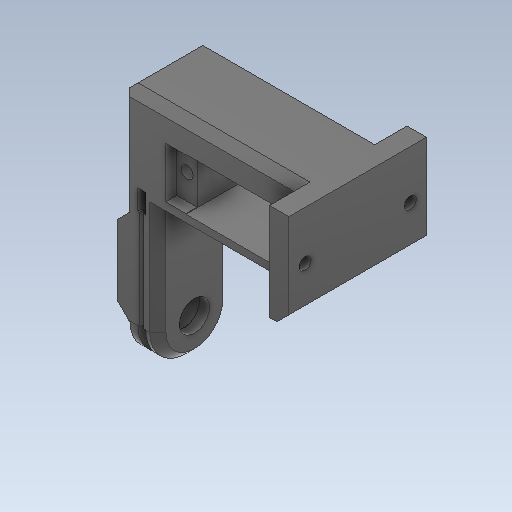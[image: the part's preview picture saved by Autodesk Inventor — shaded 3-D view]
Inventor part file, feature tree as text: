
AUTODESK INVENTOR PART (.ipt)
format: ipt  version: 2020 (Build 240168000, 168)  size: 919,552 bytes
history: native  units: mm
features: extrude x39, sketch x38, projected_geometry x26, chamfer x8, reference x8, other x5, plane x1, hole x1
ambient origin geometry x8: Origin, YZ Plane, XZ Plane, XY Plane, X Axis, Y Axis, Z Axis, Center Point
bodies: Solid1 (feature_tree)
feature tree (126):
  extrude  "Extrusion1"  Depth=45.0mm
  plane  "Work Plane1"
  extrude  "Extrusion2"  Depth=18.0mm
  extrude  "Extrusion3"  Depth=51.1mm TaperAngle=0.0deg
  extrude  "Extrusion4"  TaperAngle=0.0deg  [1 undecoded]
  extrude  "Extrusion5"  Depth=50.1mm TaperAngle=0.0deg
  sketch  "Sketch6"  dims[d14=7.199887mm d15=3.599976mm]
  extrude  "Extrusion6"  Depth=3.599976mm
  extrude  "Extrusion7"  Depth=0.15mm
  extrude  "Extrusion8"  Depth=0.15mm
  extrude  "Extrusion10"  Depth=15.9mm TaperAngle=0.0deg
  extrude  "Extrusion11"  Depth=23.15mm
  extrude  "Extrusion12"  Depth=3.925mm
  extrude  "Extrusion13"  Depth=5.15mm
  sketch  "Sketch14"  dims[d29=2.525mm d30=5.15mm]
  extrude  "Extrusion14"  Depth=12.55mm
  extrude  "Extrusion15"  Depth=2.75mm TaperAngle=0.0deg
  hole  "Hole1"  [1 undecoded]
  extrude  "Extrusion16"  Depth=2.525mm
  extrude  "Extrusion18"  Depth=23.15mm
  extrude  "Extrusion20"  Depth=10.0mm
  extrude  "Extrusion21"  Depth=0.0mm
  extrude  "Extrusion22"  TaperAngle=0.0deg  [1 undecoded]
  chamfer  "Chamfer1"  Distance=12.55mm
  chamfer  "Chamfer2"  Distance=4.0mm
  extrude  "Extrusion25"  Depth=3.85mm
  extrude  "Extrusion26"  Depth=0.765mm
  extrude  "Extrusion28"  Depth=18.0mm
  extrude  "Extrusion31"  Depth=5.0mm
  extrude  "Extrusion32"  Depth=53.1mm TaperAngle=0.0deg
  extrude  "Extrusion35"  Depth=10.0mm
  extrude  "Extrusion36"  Depth=10.0mm TaperAngle=0.0deg
  extrude  "Extrusion37"  Depth=10.0mm
  extrude  "Extrusion38"  Depth=10.0mm TaperAngle=0.0deg
  extrude  "Extrusion40"  Depth=10.0mm
  extrude  "Extrusion41"  Depth=10.0mm
  extrude  "Extrusion42"  Depth=10.0mm
  chamfer  "Chamfer5"  Distance=26.0mm
  extrude  "Extrusion43"  Depth=10.0mm
  extrude  "Extrusion44"  Depth=10.0mm
  chamfer  "Chamfer6"  Distance=4.0mm
  chamfer  "Chamfer7"  Distance=12.0mm
  extrude  "Extrusion45"  Depth=10.0mm TaperAngle=0.0deg
  extrude  "Extrusion46"  Depth=10.0mm TaperAngle=0.0deg
  extrude  "Extrusion47"  Depth=10.0mm
  chamfer  "Chamfer8"  Distance=15.292019mm
  chamfer  "Chamfer9"  Distance=67.65mm
  chamfer  "Chamfer11"  Distance=3.0mm Angle=45.0deg
  extrude  "Extrusion48"  Depth=10.0mm TaperAngle=45.0deg
  extrude  "Extrusion49"  Depth=10.0mm
  extrude  "Extrusion50"  Depth=10.0mm TaperAngle=0.0deg
  sketch  "Sketch1"  dims[d0=18.0mm d1=45.0mm]
  reference  "Reference1"
  sketch  "Sketch2"  dims[d2=45.0mm d3=18.0mm]
  reference  "Reference2"
  sketch  "Sketch3"  dims[d4=18.0mm d5=51.1mm d6=2.0mm d7=0.0mm d8=0.0mm]
  reference  "Reference3"
  reference  "Reference4"
  reference  "Reference5"
  reference  "Reference6"
  reference  "Reference7"
  reference  "Reference8"
  sketch  "Sketch4"  dims[d9=37.3mm d10=0.0mm]
  sketch  "Sketch5"  dims[d11=35.0mm d12=50.1mm d13=0.0mm]
  sketch  "Sketch8"  dims[d16=0.15mm d17=0.15mm]
  sketch  "Sketch10"  dims[d18=0.15mm d19=0.15mm]
  sketch  "Sketch11"  dims[d20=5.4mm d21=0.0mm d22=15.9mm d23=0.0mm]
  sketch  "Sketch12"  dims[d24=6.5mm d25=0.0mm d26=23.15mm]
  sketch  "Sketch13"  dims[d27=12.55mm d28=3.925mm]
  sketch  "Sketch15"  dims[d31=5.15mm d32=12.55mm]
  sketch  "Sketch17"  dims[d33=40.75mm d34=0.0mm d35=2.75mm d36=0.0mm]
  sketch  "Sketch19"  dims[d43=11.85mm d44=23.15mm]
  projected_geometry  "Projected Loop1"
  sketch  "Sketch21"  dims[d45=3.925mm d46=2.525mm]
  projected_geometry  "Projected Loop3"
  sketch  "Sketch22"  dims[d47=12.55mm d48=23.15mm]
  sketch  "Sketch23"  dims[d49=10.05mm d50=0.0mm d54=10.0mm]
  projected_geometry  "Projected Loop4"
  projected_geometry  "Projected Loop5"
  projected_geometry  "Projected Loop6"
  projected_geometry  "Projected Loop7"
  sketch  "Sketch26"  dims[d55=0.0mm d56=0.0mm]
  projected_geometry  "Projected Loop13"
  sketch  "Sketch27"  dims[d57=19.0mm d58=0.0mm]
  projected_geometry  "Projected Loop14"
  sketch  "Sketch29"  dims[d59=8.8mm]
  projected_geometry  "Projected Loop16"
  sketch  "Sketch32"  dims[d60=5.925mm]
  projected_geometry  "Projected Loop19"
  sketch  "Sketch33"  dims[d61=2.525mm]
  projected_geometry  "Projected Loop20"
  sketch  "Sketch36"  dims[d62=23.15mm]
  projected_geometry  "Projected Loop23"
  sketch  "Sketch37"  dims[d63=15.075mm]
  projected_geometry  "Projected Loop24"
  sketch  "Sketch38"  dims[d64=23.15mm]
  projected_geometry  "Projected Loop25"
  sketch  "Sketch39"  dims[d65=6.05mm]
  projected_geometry  "Projected Loop26"
  sketch  "Sketch41"  dims[d66=23.15mm d67=12.55mm d68=0.0mm]
  projected_geometry  "Projected Loop28"
  sketch  "Sketch42"  dims[d72=8.8mm]
  projected_geometry  "Projected Loop29"
  sketch  "Sketch43"  dims[d73=10.0mm]
  projected_geometry  "Projected Loop30"
  projected_geometry  "Projected Loop31"
  sketch  "Sketch44"  dims[d74=10.2mm]
  sketch  "Sketch45"  dims[d75=17.225mm d76=4.0mm d77=0.0mm]
  projected_geometry  "Projected Loop32"
  projected_geometry  "Projected Loop33"
  projected_geometry  "Projected Loop34"
  sketch  "Sketch46"  dims[d78=3.85mm d79=10.925mm]
  projected_geometry  "Projected Loop35"
  sketch  "Sketch47"  dims[d80=5.0mm d81=0.0mm d82=0.765mm]
  projected_geometry  "Projected Loop36"
  sketch  "Sketch48"  dims[d83=2.7mm d84=0.0mm d85=18.0mm]
  projected_geometry  "Projected Loop37"
  sketch  "Sketch49"  dims[d86=5.0mm d87=5.0mm]
  sketch  "Sketch50"  dims[d88=53.1mm d89=0.0mm d90=53.1mm d91=0.0mm]
  projected_geometry  "Projected Loop38"
  sketch  "Sketch51"  dims[d92=3.0mm d93=6.0mm d94=4.0mm d95=2.0mm d96=90.0deg d97=40.0mm d98=0.0mm d99=3.1mm d100=2.4mm d101=0.0mm d105=3.1mm d106=2.4mm d107=0.0mm d112=8.0mm d113=24.0mm d114=3.0mm d115=26.0mm d116=3.0mm d117=4.0mm d118=4.0mm d119=12.0mm d120=10.0mm d121=0.0mm d124=2.4mm d125=0.0mm d126=37.142391mm d127=15.292019mm d128=67.65mm d129=0.0mm d130=3.0mm d131=2.0mm d132=45.0deg d197=2.0mm d198=2.0mm d199=45.0deg d200=7.0mm d201=7.0mm d202=0.0mm d203=6.0mm d204=0.0mm d211=5.0mm d212=0.0mm d225=7.0mm d226=3.0mm d227=19.5mm d228=0.0mm d229=7.0mm d230=2.0mm d231=0.0mm d238=36.05mm d239=30.324982mm d240=68.0mm d241=0.0mm d242=7.0mm d243=7.0mm d244=10.0mm d245=0.0mm d246=10.0mm d247=0.0mm d248=2.5mm d249=1.0mm d250=1.0mm d251=10.0mm d252=0.0mm d255=27.0mm d256=1.0mm d257=2.0mm d258=2.5mm d259=0.0mm d260=27.0mm d261=1.0mm d262=2.0mm d263=90.0deg d264=90.0deg d265=2.5mm d266=0.0mm d270=9.0mm d271=0.0mm d272=2.5mm d273=2.0mm d274=45.0deg d275=2.5mm d276=2.0mm d277=0.0mm d278=2.0mm d279=1.0mm d280=4.0mm d281=0.5mm d282=90.0deg d283=0.5mm d284=2.0mm d285=0.0mm d286=2.0mm d287=2.0mm d288=45.0deg d289=2.0mm d290=2.0mm d291=45.0deg d292=5.0mm d293=20.0mm d294=0.5mm d295=0.5mm d296=90.0deg d297=1.0mm d298=0.0mm d299=5.0mm d300=0.5mm d301=90.0deg d302=0.5mm d303=90.0deg d304=1.0mm d305=0.0mm d306=3.0mm d307=20.475036mm d308=7.0mm d309=0.0mm d310=7.0mm d311=2.0mm d312=45.0deg d313=1.0mm d314=2.0mm d315=45.0deg d319=2.0mm d320=2.0mm d321=45.0deg d322=0.15mm d323=0.15mm d324=0.15mm d325=0.15mm d326=10.0mm d327=0.0mm d328=0.1mm d329=0.1mm d330=10.0mm d331=0.0mm d332=10.8mm d333=0.0mm d108=0.5mm d109=0.872665mm d148=0.5mm d149=0.872665mm d150=0.5mm d151=0.872665mm d334=0.5mm d335=0.872665mm]
  parser-record x1  (decoder bookkeeping rows leaked as tree rows — omitted from the tree; the rows remain in map.json)
  other  "Demo2.0004.iam"
  other  "Bearing:2"
  other  "Rolling bearing GB/T 7218-1995 Type FSN 70000-Z F 623-Z:1"
  other  "servo horn 1:1"
note: 3 required parameter values undecoded (feature->parameter linkage not recoverable at this tier; creation-order binding heuristic only, values carry confidence <= 0.55)
note: 1 file-system path scrubbed to <path> (originals preserved in map.json)
